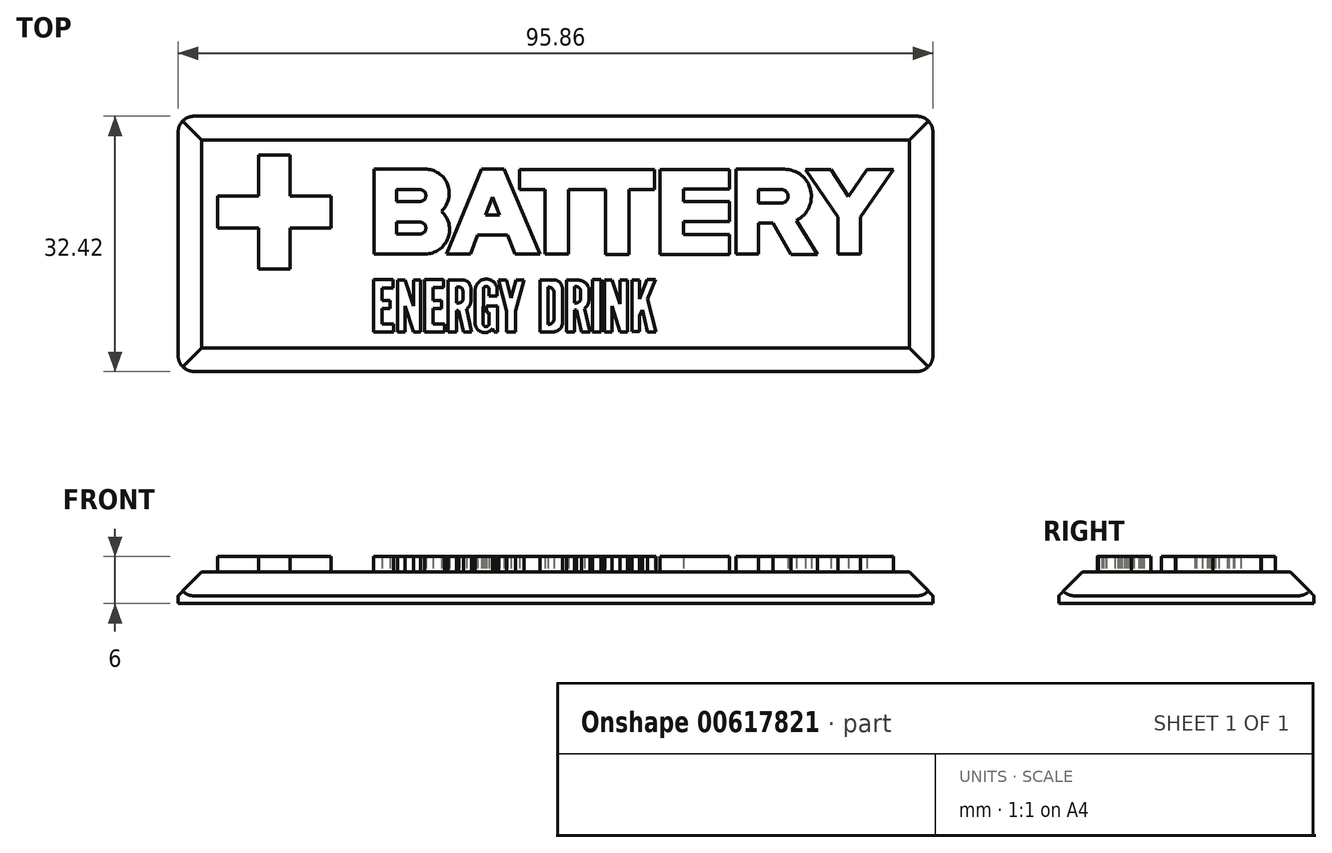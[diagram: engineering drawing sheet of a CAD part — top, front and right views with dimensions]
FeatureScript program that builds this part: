
annotation { "Feature Type Name" : "Feature", "Feature Type Description" : "" }
export const myFeature = defineFeature(function(context is Context, id is Id, definition is map)
    precondition{}
    {
        {
            var Q0;
            Q0=qCreatedBy(makeId("Top.planeOp"),FACE);
            var sketch = newSketch(context, id + "F0", { "sketchPlane" : qUnion([Q0])});
            skLineSegment(sketch, "E0", {"start": v(10.69, -9.1) * mm, "end": v(10.69, -11.17) * mm});
            skLineSegment(sketch, "E1", {"start": v(11.64, -4.52) * mm, "end": v(10.69, -7) * mm});
            skLineSegment(sketch, "E2", {"start": v(12.67, -4.52) * mm, "end": v(11.64, -4.52) * mm});
            skLineSegment(sketch, "E3", {"start": v(11.69, -7) * mm, "end": v(12.67, -4.52) * mm});
            skLineSegment(sketch, "E4", {"start": v(12.77, -11.18) * mm, "end": v(11.69, -7) * mm});
            skLineSegment(sketch, "E5", {"start": v(11.71, -11.18) * mm, "end": v(12.77, -11.18) * mm});
            skLineSegment(sketch, "E6", {"start": v(-14.22, -4.56) * mm, "end": v(-14.22, -5.55) * mm});
            skLineSegment(sketch, "E7", {"start": v(-15.55, -5.55) * mm, "end": v(-14.22, -5.55) * mm});
            skLineSegment(sketch, "E8", {"start": v(-15.55, -4.56) * mm, "end": v(-14.22, -4.56) * mm});
            skLineSegment(sketch, "E9", {"start": v(-15.55, -10.18) * mm, "end": v(-15.55, -8.23) * mm});
            skLineSegment(sketch, "E10", {"start": v(-16.65, -11.2) * mm, "end": v(-16.65, -4.56) * mm});
            skLineSegment(sketch, "E11", {"start": v(-16.65, -4.56) * mm, "end": v(-15.55, -4.56) * mm});
            skLineSegment(sketch, "E12", {"start": v(-16.65, -11.2) * mm, "end": v(-15.55, -11.2) * mm});
            skLineSegment(sketch, "E13", {"start": v(-22, -7.22) * mm, "end": v(-22, -5.58) * mm});
            skLineSegment(sketch, "E14", {"start": v(-18.07, -11.18) * mm, "end": v(-19.11, -7.88) * mm});
            skLineSegment(sketch, "E15", {"start": v(-19.11, -4.58) * mm, "end": v(-18.07, -7.88) * mm});
            skLineSegment(sketch, "E16", {"start": v(-17.12, -4.58) * mm, "end": v(-17.12, -11.18) * mm});
            skLineSegment(sketch, "E17", {"start": v(-18.07, -4.58) * mm, "end": v(-18.07, -7.88) * mm});
            skLineSegment(sketch, "E18", {"start": v(-18.07, -11.18) * mm, "end": v(-17.12, -11.18) * mm});
            skLineSegment(sketch, "E19", {"start": v(-18.07, -4.58) * mm, "end": v(-17.12, -4.58) * mm});
            skLineSegment(sketch, "E20", {"start": v(-20.06, -11.2) * mm, "end": v(-20.06, -4.58) * mm});
            skLineSegment(sketch, "E21", {"start": v(-19.11, -11.2) * mm, "end": v(-19.11, -7.88) * mm});
            skLineSegment(sketch, "E22", {"start": v(-19.11, -4.58) * mm, "end": v(-20.06, -4.58) * mm});
            skLineSegment(sketch, "E23", {"start": v(-19.11, -11.2) * mm, "end": v(-20.06, -11.2) * mm});
            skLineSegment(sketch, "E24", {"start": v(-20.6, -10.2) * mm, "end": v(-20.6, -11.2) * mm});
            skLineSegment(sketch, "E25", {"start": v(-22, -11.2) * mm, "end": v(-20.6, -11.2) * mm});
            skLineSegment(sketch, "E26", {"start": v(-22, -10.2) * mm, "end": v(-20.6, -10.2) * mm});
            skLineSegment(sketch, "E27", {"start": v(-21, -7.22) * mm, "end": v(-21, -8.23) * mm});
            skLineSegment(sketch, "E28", {"start": v(-22, -8.23) * mm, "end": v(-21, -8.23) * mm});
            skLineSegment(sketch, "E29", {"start": v(-22, -7.22) * mm, "end": v(-21, -7.22) * mm});
            skLineSegment(sketch, "E30", {"start": v(-20.64, -4.54) * mm, "end": v(-20.64, -5.58) * mm});
            skLineSegment(sketch, "E31", {"start": v(-22, -5.58) * mm, "end": v(-20.64, -5.58) * mm});
            skLineSegment(sketch, "E32", {"start": v(-22, -4.54) * mm, "end": v(-20.64, -4.54) * mm});
            skLineSegment(sketch, "E33", {"start": v(-22, -10.2) * mm, "end": v(-22, -8.23) * mm});
            skLineSegment(sketch, "E34", {"start": v(-23.13, -11.2) * mm, "end": v(-23.13, -4.54) * mm});
            skLineSegment(sketch, "E35", {"start": v(-23.13, -4.54) * mm, "end": v(-22, -4.54) * mm});
            skLineSegment(sketch, "E36", {"start": v(-23.13, -11.2) * mm, "end": v(-22, -11.2) * mm});
            skLineSegment(sketch, "E37", {"start": v(42.93, 9.45) * mm, "end": v(38.76, 3.38) * mm});
            skLineSegment(sketch, "E38", {"start": v(39.57, 9.45) * mm, "end": v(42.93, 9.45) * mm});
            skLineSegment(sketch, "E39", {"start": v(37.24, 6.03) * mm, "end": v(39.57, 9.45) * mm});
            skLineSegment(sketch, "E40", {"start": v(34.99, 9.43) * mm, "end": v(37.24, 6.03) * mm});
            skLineSegment(sketch, "E41", {"start": v(31.74, 9.43) * mm, "end": v(34.99, 9.43) * mm});
            skLineSegment(sketch, "E42", {"start": v(35.85, 3.38) * mm, "end": v(31.74, 9.43) * mm});
            skLineSegment(sketch, "E43", {"start": v(38.76, -1.31) * mm, "end": v(38.76, 3.38) * mm});
            skLineSegment(sketch, "E44", {"start": v(35.85, -1.31) * mm, "end": v(35.85, 3.38) * mm});
            skLineSegment(sketch, "E45", {"start": v(35.85, -1.31) * mm, "end": v(38.76, -1.31) * mm});
            skLineSegment(sketch, "E46", {"start": v(16.23, 5.4) * mm, "end": v(16.23, 6.94) * mm});
            skLineSegment(sketch, "E47", {"start": v(25.79, 2.66) * mm, "end": v(25.79, -1.3) * mm});
            skArc(sketch, "E48", {"start": v(30.6, 2.98) * mm, "mid": v(32.41, 6.83) * mm, "end": v(29.07, 9.47) * mm});
            skArc(sketch, "E49", {"start": v(28.7, 5.19) * mm, "mid": v(29.55, 6.04) * mm, "end": v(28.7, 6.89) * mm});
            skLineSegment(sketch, "E50", {"start": v(25.79, 9.47) * mm, "end": v(29.07, 9.47) * mm});
            skLineSegment(sketch, "E51", {"start": v(25.79, 6.89) * mm, "end": v(28.7, 6.89) * mm});
            skLineSegment(sketch, "E52", {"start": v(25.79, 5.19) * mm, "end": v(28.7, 5.19) * mm});
            skLineSegment(sketch, "E53", {"start": v(33.25, -1.36) * mm, "end": v(30.6, 2.98) * mm});
            skLineSegment(sketch, "E54", {"start": v(29.88, -1.36) * mm, "end": v(33.25, -1.36) * mm});
            skLineSegment(sketch, "E55", {"start": v(27.64, 2.66) * mm, "end": v(29.88, -1.36) * mm});
            skLineSegment(sketch, "E56", {"start": v(-1.32, 6.92) * mm, "end": v(-1.32, -1.32) * mm});
            skLineSegment(sketch, "E57", {"start": v(-1.32, -1.32) * mm, "end": v(1.64, -1.32) * mm});
            skLineSegment(sketch, "E58", {"start": v(12.57, 9.46) * mm, "end": v(12.57, 6.92) * mm});
            skLineSegment(sketch, "E59", {"start": v(-4.54, 9.46) * mm, "end": v(-4.54, 6.92) * mm});
            skLineSegment(sketch, "E60", {"start": v(-4.54, 6.92) * mm, "end": v(-1.32, 6.92) * mm});
            skLineSegment(sketch, "E61", {"start": v(-4.54, 9.46) * mm, "end": v(12.57, 9.46) * mm});
            skLineSegment(sketch, "E62", {"start": v(-8, 5.96) * mm, "end": v(-8.9, 3.66) * mm});
            skLineSegment(sketch, "E63", {"start": v(-7.12, 3.66) * mm, "end": v(-8, 5.96) * mm});
            skLineSegment(sketch, "E64", {"start": v(-8.9, 3.66) * mm, "end": v(-7.12, 3.66) * mm});
            skLineSegment(sketch, "E65", {"start": v(-9.36, 9.47) * mm, "end": v(-13.84, -1.29) * mm});
            skLineSegment(sketch, "E66", {"start": v(-6.55, 9.47) * mm, "end": v(-9.36, 9.47) * mm});
            skLineSegment(sketch, "E67", {"start": v(-1.94, -1.29) * mm, "end": v(-6.55, 9.47) * mm});
            skLineSegment(sketch, "E68", {"start": v(-20.16, 2.77) * mm, "end": v(-17.23, 2.77) * mm});
            skLineSegment(sketch, "E69", {"start": v(-20.16, 1.24) * mm, "end": v(-17.23, 1.24) * mm});
            skLineSegment(sketch, "E70", {"start": v(-20.16, 2.77) * mm, "end": v(-20.16, 1.24) * mm});
            skArc(sketch, "E71", {"start": v(-17.23, 5.37) * mm, "mid": v(-16.47, 6.13) * mm, "end": v(-17.23, 6.9) * mm});
            skArc(sketch, "E72", {"start": v(-17.23, 1.24) * mm, "mid": v(-16.47, 2) * mm, "end": v(-17.23, 2.77) * mm});
            skLineSegment(sketch, "E73", {"start": v(-13.84, -1.29) * mm, "end": v(-10.78, -1.29) * mm});
            skLineSegment(sketch, "E74", {"start": v(-10.78, -1.29) * mm, "end": v(-9.9, 1.1) * mm});
            skLineSegment(sketch, "E75", {"start": v(-9.9, 1.1) * mm, "end": v(-6.12, 1.1) * mm});
            skLineSegment(sketch, "E76", {"start": v(-6.12, 1.1) * mm, "end": v(-5.16, -1.29) * mm});
            skLineSegment(sketch, "E77", {"start": v(-5.16, -1.29) * mm, "end": v(-1.94, -1.29) * mm});
            skLineSegment(sketch, "E78", {"start": v(1.64, 6.92) * mm, "end": v(1.64, -1.32) * mm});
            skLineSegment(sketch, "E79", {"start": v(6.36, -1.37) * mm, "end": v(9.35, -1.37) * mm});
            skLineSegment(sketch, "E80", {"start": v(6.36, 6.92) * mm, "end": v(6.36, -1.37) * mm});
            skLineSegment(sketch, "E81", {"start": v(9.35, 6.92) * mm, "end": v(9.35, -1.37) * mm});
            skLineSegment(sketch, "E82", {"start": v(1.64, 6.92) * mm, "end": v(6.36, 6.92) * mm});
            skLineSegment(sketch, "E83", {"start": v(9.35, 6.92) * mm, "end": v(12.57, 6.92) * mm});
            skLineSegment(sketch, "E84", {"start": v(13.26, -1.37) * mm, "end": v(16.23, -1.37) * mm});
            skLineSegment(sketch, "E85", {"start": v(13.26, 9.47) * mm, "end": v(16.23, 9.47) * mm});
            skLineSegment(sketch, "E86", {"start": v(13.26, -1.37) * mm, "end": v(13.26, 9.47) * mm});
            skLineSegment(sketch, "E87", {"start": v(16.23, 1.2) * mm, "end": v(16.23, 2.87) * mm});
            skLineSegment(sketch, "E88", {"start": v(16.23, 9.47) * mm, "end": v(22.12, 9.47) * mm});
            skLineSegment(sketch, "E89", {"start": v(16.23, 6.94) * mm, "end": v(22.12, 6.94) * mm});
            skLineSegment(sketch, "E90", {"start": v(22.12, 9.47) * mm, "end": v(22.12, 6.94) * mm});
            skLineSegment(sketch, "E91", {"start": v(16.23, 5.4) * mm, "end": v(22.12, 5.4) * mm});
            skLineSegment(sketch, "E92", {"start": v(16.23, 2.87) * mm, "end": v(22.12, 2.87) * mm});
            skLineSegment(sketch, "E93", {"start": v(22.12, 5.4) * mm, "end": v(22.12, 2.87) * mm});
            skLineSegment(sketch, "E94", {"start": v(16.23, 1.2) * mm, "end": v(22.11, 1.2) * mm});
            skLineSegment(sketch, "E95", {"start": v(16.23, -1.37) * mm, "end": v(22.11, -1.37) * mm});
            skLineSegment(sketch, "E96", {"start": v(22.11, 1.2) * mm, "end": v(22.11, -1.37) * mm});
            skLineSegment(sketch, "E97", {"start": v(22.9, 9.47) * mm, "end": v(25.79, 9.47) * mm});
            skLineSegment(sketch, "E98", {"start": v(22.9, -1.3) * mm, "end": v(25.79, -1.3) * mm});
            skLineSegment(sketch, "E99", {"start": v(22.9, 9.47) * mm, "end": v(22.9, -1.3) * mm});
            skLineSegment(sketch, "E100", {"start": v(25.79, 6.89) * mm, "end": v(25.79, 5.19) * mm});
            skLineSegment(sketch, "E101", {"start": v(25.79, 2.66) * mm, "end": v(27.64, 2.66) * mm});
            skLineSegment(sketch, "E102", {"start": v(-15.55, -7.2) * mm, "end": v(-14.5, -7.2) * mm});
            skLineSegment(sketch, "E103", {"start": v(-15.55, -8.23) * mm, "end": v(-14.5, -8.23) * mm});
            skLineSegment(sketch, "E104", {"start": v(-14.5, -7.2) * mm, "end": v(-14.5, -8.23) * mm});
            skLineSegment(sketch, "E105", {"start": v(-15.55, -10.18) * mm, "end": v(-14.1, -10.18) * mm});
            skLineSegment(sketch, "E106", {"start": v(-15.58, -11.2) * mm, "end": v(-14.1, -11.2) * mm});
            skLineSegment(sketch, "E107", {"start": v(-14.1, -10.18) * mm, "end": v(-14.1, -11.2) * mm});
            skLineSegment(sketch, "E108", {"start": v(-15.55, -7.2) * mm, "end": v(-15.55, -5.55) * mm});
            skLineSegment(sketch, "E109", {"start": v(-13.67, -11.19) * mm, "end": v(-12.6, -11.19) * mm});
            skLineSegment(sketch, "E110", {"start": v(-13.67, -4.57) * mm, "end": v(-12.6, -4.57) * mm});
            skLineSegment(sketch, "E111", {"start": v(-13.67, -11.19) * mm, "end": v(-13.67, -4.57) * mm});
            skLineSegment(sketch, "E112", {"start": v(-12.6, -11.19) * mm, "end": v(-12.6, -8.44) * mm});
            skLineSegment(sketch, "E113", {"start": v(-12.6, -8.44) * mm, "end": v(-12.33, -8.44) * mm});
            skLineSegment(sketch, "E114", {"start": v(-12.33, -8.44) * mm, "end": v(-11.72, -11.2) * mm});
            skLineSegment(sketch, "E115", {"start": v(-11.72, -11.2) * mm, "end": v(-10.64, -11.2) * mm});
            skLineSegment(sketch, "E116", {"start": v(-10.64, -11.2) * mm, "end": v(-11.32, -8.23) * mm});
            skLineSegment(sketch, "E117", {"start": v(-12.6, -5.5) * mm, "end": v(-12.2, -5.5) * mm});
            skLineSegment(sketch, "E118", {"start": v(-12.6, -7.49) * mm, "end": v(-12.2, -7.49) * mm});
            skLineSegment(sketch, "E119", {"start": v(-12.6, -4.57) * mm, "end": v(-11.87, -4.57) * mm});
            skLineSegment(sketch, "E120", {"start": v(-11.78, -5.95) * mm, "end": v(-11.78, -6.97) * mm});
            skLineSegment(sketch, "E121", {"start": v(-10.75, -5.57) * mm, "end": v(-10.75, -7.26) * mm});
            skArc(sketch, "E122", {"start": v(-11.78, -5.95) * mm, "mid": v(-11.9, -5.64) * mm, "end": v(-12.2, -5.5) * mm});
            skArc(sketch, "E123", {"start": v(-12.2, -7.49) * mm, "mid": v(-11.87, -7.33) * mm, "end": v(-11.78, -6.97) * mm});
            skArc(sketch, "E124", {"start": v(-10.75, -5.57) * mm, "mid": v(-11.12, -4.86) * mm, "end": v(-11.87, -4.57) * mm});
            skArc(sketch, "E125", {"start": v(-11.32, -8.23) * mm, "mid": v(-10.9, -7.82) * mm, "end": v(-10.75, -7.26) * mm});
            skLineSegment(sketch, "E126", {"start": v(-10.2, -6.03) * mm, "end": v(-10.22, -10.06) * mm});
            skLineSegment(sketch, "E127", {"start": v(-9.17, -5.76) * mm, "end": v(-9.2, -10.14) * mm});
            skLineSegment(sketch, "E128", {"start": v(-8.43, -6.65) * mm, "end": v(-7.4, -6.65) * mm});
            skLineSegment(sketch, "E129", {"start": v(-8.43, -6.65) * mm, "end": v(-8.43, -5.76) * mm});
            skLineSegment(sketch, "E130", {"start": v(-7.4, -6.65) * mm, "end": v(-7.4, -5.89) * mm});
            skLineSegment(sketch, "E131", {"start": v(-8.78, -7.87) * mm, "end": v(-7.37, -7.87) * mm});
            skLineSegment(sketch, "E132", {"start": v(-8.78, -7.87) * mm, "end": v(-8.78, -8.72) * mm});
            skLineSegment(sketch, "E133", {"start": v(-7.37, -7.87) * mm, "end": v(-7.37, -8.72) * mm});
            skLineSegment(sketch, "E134", {"start": v(-7.37, -8.72) * mm, "end": v(-7.37, -10.14) * mm});
            skLineSegment(sketch, "E135", {"start": v(-8.44, -8.72) * mm, "end": v(-8.44, -10.14) * mm});
            skLineSegment(sketch, "E136", {"start": v(-7.8, -11.17) * mm, "end": v(-7.37, -11.17) * mm});
            skLineSegment(sketch, "E137", {"start": v(-7.37, -11.17) * mm, "end": v(-7.37, -10.14) * mm});
            skLineSegment(sketch, "E138", {"start": v(-7.8, -11.17) * mm, "end": v(-8, -10.74) * mm});
            skArc(sketch, "E139", {"start": v(-8.43, -5.76) * mm, "mid": v(-8.8, -5.39) * mm, "end": v(-9.17, -5.76) * mm});
            skArc(sketch, "E140", {"start": v(-7.4, -5.89) * mm, "mid": v(-8.88, -4.49) * mm, "end": v(-10.2, -6.03) * mm});
            skArc(sketch, "E141", {"start": v(-10.22, -10.06) * mm, "mid": v(-9.36, -11.23) * mm, "end": v(-8, -10.74) * mm});
            skArc(sketch, "E142", {"start": v(-9.2, -10.14) * mm, "mid": v(-8.81, -10.52) * mm, "end": v(-8.44, -10.14) * mm});
            skLineSegment(sketch, "E143", {"start": v(-12.6, -7.49) * mm, "end": v(-12.6, -5.5) * mm});
            skLineSegment(sketch, "E144", {"start": v(-8.78, -8.72) * mm, "end": v(-8.44, -8.72) * mm});
            skLineSegment(sketch, "E145", {"start": v(-6.21, -11.18) * mm, "end": v(-5.07, -11.18) * mm});
            skLineSegment(sketch, "E146", {"start": v(-6.21, -11.18) * mm, "end": v(-6.21, -8.52) * mm});
            skLineSegment(sketch, "E147", {"start": v(-5.07, -11.18) * mm, "end": v(-5.07, -8.52) * mm});
            skLineSegment(sketch, "E148", {"start": v(-6.21, -8.52) * mm, "end": v(-7.26, -4.6) * mm});
            skLineSegment(sketch, "E149", {"start": v(-7.26, -4.6) * mm, "end": v(-6.21, -4.6) * mm});
            skLineSegment(sketch, "E150", {"start": v(-6.21, -4.6) * mm, "end": v(-5.67, -6.88) * mm});
            skLineSegment(sketch, "E151", {"start": v(-5.67, -6.88) * mm, "end": v(-5.02, -4.57) * mm});
            skLineSegment(sketch, "E152", {"start": v(-5.02, -4.57) * mm, "end": v(-3.98, -4.57) * mm});
            skLineSegment(sketch, "E153", {"start": v(-3.98, -4.57) * mm, "end": v(-5.07, -8.52) * mm});
            skLineSegment(sketch, "E154", {"start": v(-1.98, -4.56) * mm, "end": v(-0.94, -4.56) * mm});
            skLineSegment(sketch, "E155", {"start": v(-1.98, -11.18) * mm, "end": v(-0.94, -11.18) * mm});
            skLineSegment(sketch, "E156", {"start": v(-1.98, -4.56) * mm, "end": v(-1.98, -11.18) * mm});
            skLineSegment(sketch, "E157", {"start": v(-0.94, -5.5) * mm, "end": v(-0.94, -10.22) * mm});
            skLineSegment(sketch, "E158", {"start": v(-0.2, -6.2) * mm, "end": v(-0.2, -9.54) * mm});
            skLineSegment(sketch, "E159", {"start": v(0.87, -5.81) * mm, "end": v(0.87, -10.19) * mm});
            skLineSegment(sketch, "E160", {"start": v(-0.94, -4.56) * mm, "end": v(-0.27, -4.56) * mm});
            skLineSegment(sketch, "E161", {"start": v(-0.94, -11.18) * mm, "end": v(-0.29, -11.18) * mm});
            skArc(sketch, "E162", {"start": v(-0.2, -6.2) * mm, "mid": v(-0.42, -5.68) * mm, "end": v(-0.94, -5.5) * mm});
            skArc(sketch, "E163", {"start": v(-0.94, -10.22) * mm, "mid": v(-0.42, -10.05) * mm, "end": v(-0.2, -9.54) * mm});
            skArc(sketch, "E164", {"start": v(0.87, -5.81) * mm, "mid": v(0.57, -4.94) * mm, "end": v(-0.27, -4.56) * mm});
            skArc(sketch, "E165", {"start": v(-0.29, -11.18) * mm, "mid": v(0.48, -10.9) * mm, "end": v(0.87, -10.19) * mm});
            skLineSegment(sketch, "E166", {"start": v(1.38, -4.61) * mm, "end": v(2.4, -4.61) * mm});
            skLineSegment(sketch, "E167", {"start": v(1.38, -11.2) * mm, "end": v(2.4, -11.2) * mm});
            skLineSegment(sketch, "E168", {"start": v(1.38, -4.61) * mm, "end": v(1.38, -11.2) * mm});
            skLineSegment(sketch, "E169", {"start": v(2.4, -5.45) * mm, "end": v(2.4, -7.5) * mm});
            skLineSegment(sketch, "E170", {"start": v(2.4, -8.4) * mm, "end": v(2.68, -8.4) * mm});
            skLineSegment(sketch, "E171", {"start": v(2.68, -8.4) * mm, "end": v(3.28, -11.18) * mm});
            skLineSegment(sketch, "E172", {"start": v(3.28, -11.18) * mm, "end": v(4.39, -11.18) * mm});
            skLineSegment(sketch, "E173", {"start": v(4.39, -11.18) * mm, "end": v(3.67, -8.2) * mm});
            skLineSegment(sketch, "E174", {"start": v(2.4, -5.45) * mm, "end": v(2.72, -5.45) * mm});
            skLineSegment(sketch, "E175", {"start": v(2.4, -7.5) * mm, "end": v(2.74, -7.5) * mm});
            skLineSegment(sketch, "E176", {"start": v(3.18, -5.97) * mm, "end": v(3.18, -6.98) * mm});
            skLineSegment(sketch, "E177", {"start": v(2.4, -4.61) * mm, "end": v(2.9, -4.61) * mm});
            skArc(sketch, "E178", {"start": v(3.18, -5.97) * mm, "mid": v(3.05, -5.62) * mm, "end": v(2.72, -5.45) * mm});
            skArc(sketch, "E179", {"start": v(2.74, -7.5) * mm, "mid": v(3.06, -7.32) * mm, "end": v(3.18, -6.98) * mm});
            skArc(sketch, "E180", {"start": v(4.23, -5.62) * mm, "mid": v(3.74, -4.9) * mm, "end": v(2.9, -4.61) * mm});
            skLineSegment(sketch, "E181", {"start": v(4.23, -5.62) * mm, "end": v(4.23, -7.16) * mm});
            skArc(sketch, "E182", {"start": v(3.67, -8.2) * mm, "mid": v(4.08, -7.75) * mm, "end": v(4.23, -7.16) * mm});
            skLineSegment(sketch, "E183", {"start": v(2.4, -8.4) * mm, "end": v(2.4, -11.2) * mm});
            skLineSegment(sketch, "E184", {"start": v(4.67, -4.52) * mm, "end": v(5.77, -4.52) * mm});
            skLineSegment(sketch, "E185", {"start": v(4.67, -11.2) * mm, "end": v(5.77, -11.2) * mm});
            skLineSegment(sketch, "E186", {"start": v(4.67, -4.52) * mm, "end": v(4.67, -11.2) * mm});
            skLineSegment(sketch, "E187", {"start": v(5.77, -4.52) * mm, "end": v(5.77, -11.2) * mm});
            skLineSegment(sketch, "E188", {"start": v(6.23, -4.57) * mm, "end": v(7.19, -4.57) * mm});
            skLineSegment(sketch, "E189", {"start": v(6.23, -11.2) * mm, "end": v(7.19, -11.2) * mm});
            skLineSegment(sketch, "E190", {"start": v(6.23, -4.57) * mm, "end": v(6.23, -11.2) * mm});
            skLineSegment(sketch, "E191", {"start": v(7.19, -7.89) * mm, "end": v(7.19, -11.2) * mm});
            skLineSegment(sketch, "E192", {"start": v(9.12, -11.18) * mm, "end": v(8.18, -11.18) * mm});
            skLineSegment(sketch, "E193", {"start": v(9.12, -4.57) * mm, "end": v(8.18, -4.57) * mm});
            skLineSegment(sketch, "E194", {"start": v(9.12, -11.18) * mm, "end": v(9.12, -4.57) * mm});
            skLineSegment(sketch, "E195", {"start": v(8.18, -7.67) * mm, "end": v(8.18, -4.57) * mm});
            skLineSegment(sketch, "E196", {"start": v(7.19, -4.57) * mm, "end": v(8.18, -7.67) * mm});
            skLineSegment(sketch, "E197", {"start": v(8.18, -11.18) * mm, "end": v(7.19, -7.89) * mm});
            skLineSegment(sketch, "E198", {"start": v(9.7, -4.6) * mm, "end": v(10.69, -4.6) * mm});
            skLineSegment(sketch, "E199", {"start": v(9.7, -11.17) * mm, "end": v(10.69, -11.17) * mm});
            skLineSegment(sketch, "E200", {"start": v(9.7, -4.6) * mm, "end": v(9.7, -11.17) * mm});
            skLineSegment(sketch, "E201", {"start": v(10.69, -4.6) * mm, "end": v(10.69, -7) * mm});
            skLineSegment(sketch, "E202", {"start": v(10.69, -9.1) * mm, "end": v(11.03, -8.39) * mm});
            skLineSegment(sketch, "E203", {"start": v(11.03, -8.39) * mm, "end": v(11.71, -11.18) * mm});
            skLineSegment(sketch, "E204", {"start": v(-37.74, 11.28) * mm, "end": v(-33.7, 11.28) * mm});
            skLineSegment(sketch, "E205", {"start": v(-37.74, -3.17) * mm, "end": v(-33.7, -3.17) * mm});
            skLineSegment(sketch, "E206", {"start": v(-37.74, 11.28) * mm, "end": v(-37.74, 6.07) * mm});
            skLineSegment(sketch, "E207", {"start": v(-33.7, 11.28) * mm, "end": v(-33.7, 6.07) * mm});
            skLineSegment(sketch, "E208", {"start": v(-42.93, 6.07) * mm, "end": v(-37.74, 6.07) * mm});
            skLineSegment(sketch, "E209", {"start": v(-42.93, 2.01) * mm, "end": v(-37.74, 2.01) * mm});
            skLineSegment(sketch, "E210", {"start": v(-42.93, 6.07) * mm, "end": v(-42.93, 2.01) * mm});
            skLineSegment(sketch, "E211", {"start": v(-28.5, 6.07) * mm, "end": v(-28.5, 2.01) * mm});
            skLineSegment(sketch, "E212", {"start": v(-33.7, 6.07) * mm, "end": v(-28.5, 6.07) * mm});
            skLineSegment(sketch, "E213", {"start": v(-37.74, 2.01) * mm, "end": v(-37.74, -3.17) * mm});
            skLineSegment(sketch, "E214", {"start": v(-33.7, 2.01) * mm, "end": v(-33.7, -3.17) * mm});
            skLineSegment(sketch, "E215", {"start": v(-33.7, 2.01) * mm, "end": v(-28.5, 2.01) * mm});
            skLineSegment(sketch, "E216", {"start": v(-23.07, 9.5) * mm, "end": v(-23.07, -1.29) * mm});
            skLineSegment(sketch, "E217", {"start": v(-23.07, -1.29) * mm, "end": v(-16.57, -1.29) * mm});
            skLineSegment(sketch, "E218", {"start": v(-23.07, 9.5) * mm, "end": v(-16.57, 9.5) * mm});
            skArc(sketch, "E219", {"start": v(-14.5, 4.15) * mm, "mid": v(-13.7, 7.54) * mm, "end": v(-16.57, 9.5) * mm});
            skArc(sketch, "E220", {"start": v(-16.57, -1.29) * mm, "mid": v(-13.66, 0.72) * mm, "end": v(-14.5, 4.15) * mm});
            skLineSegment(sketch, "E221", {"start": v(-20.16, 6.9) * mm, "end": v(-20.16, 5.37) * mm});
            skLineSegment(sketch, "E222", {"start": v(-20.16, 5.37) * mm, "end": v(-17.23, 5.37) * mm});
            skLineSegment(sketch, "E223", {"start": v(-20.16, 6.9) * mm, "end": v(-17.23, 6.9) * mm});
            skSolve(sketch);
        }
        {
            var Q0;
            Q0=qCreatedBy(makeId("Top.planeOp"),FACE);
            var sketch = newSketch(context, id + "F1", { "sketchPlane" : qUnion([Q0])});
            skLineSegment(sketch, "E224.bottom", {"start": v(47.93, -16.2) * mm, "end": v(-47.93, -16.2) * mm});
            skLineSegment(sketch, "E224.top", {"start": v(47.93, 16.2) * mm, "end": v(-47.93, 16.2) * mm});
            skLineSegment(sketch, "E224.left", {"start": v(47.93, -16.2) * mm, "end": v(47.93, 16.2) * mm});
            skLineSegment(sketch, "E224.right", {"start": v(-47.93, -16.2) * mm, "end": v(-47.93, 16.2) * mm});
            skPoint(sketch, "E224.middle", {"position": v(0, 0) * mm});
            skSolve(sketch);
        }
        {
            var Q0;
            Q0 = qSketchRegion(id + "F1", true);
            extrude(context, id + "F2", {"entities" : qUnion([Q0]), "oppositeDirection" : true, "depth" : 4 * mm, "offsetDistance" : 25 * mm});
        }
        {
            var Q0;
            Q0 = qSketchRegion(id + "F0", true);
            extrude(context, id + "F3", {"entities" : qUnion([Q0]), "operationType" : NewBodyOperationType.ADD, "depth" : 2 * mm, "offsetDistance" : 25 * mm});
        }
        {
            var Q0;
            Q0=makeQuery(id+"F2.opExtrude","CAP_EDGE",EDGE,{"disambiguationData":[OSD([sQuery(id+"F1.wireOp",EDGE,"E224.bottom")])],"isStart":true});
            var Q1;
            Q1=makeQuery(id+"F2.opExtrude","CAP_EDGE",EDGE,{"disambiguationData":[OSD([sQuery(id+"F1.wireOp",EDGE,"E224.left")])],"isStart":true});
            var Q2;
            Q2=makeQuery(id+"F2.opExtrude","CAP_EDGE",EDGE,{"disambiguationData":[OSD([sQuery(id+"F1.wireOp",EDGE,"E224.top")])],"isStart":true});
            var Q3;
            Q3=makeQuery(id+"F2.opExtrude","CAP_EDGE",EDGE,{"disambiguationData":[OSD([sQuery(id+"F1.wireOp",EDGE,"E224.right")])],"isStart":true});
            chamfer(context, id + "F4", {"entities" : qUnion([Q0, Q1, Q2, Q3]), "width" : 3 * mm, "tangentPropagation" : true});
        }
        {
            var Q0;
            Q0=makeQuery(id+"F2.opExtrude","SWEPT_EDGE",EDGE,{"disambiguationData":[OSD([sQuery(id+"F1.wireOp",EDGE,"E224.top"),sQuery(id+"F1.wireOp",EDGE,"E224.right")])]});
            var Q1;
            Q1=makeQuery(id+"F2.opExtrude","SWEPT_EDGE",EDGE,{"disambiguationData":[OSD([sQuery(id+"F1.wireOp",EDGE,"E224.top"),sQuery(id+"F1.wireOp",EDGE,"E224.left")])]});
            var Q2;
            Q2=makeQuery(id+"F2.opExtrude","SWEPT_EDGE",EDGE,{"disambiguationData":[OSD([sQuery(id+"F1.wireOp",EDGE,"E224.bottom"),sQuery(id+"F1.wireOp",EDGE,"E224.left")])]});
            var Q3;
            Q3=makeQuery(id+"F2.opExtrude","SWEPT_EDGE",EDGE,{"disambiguationData":[OSD([sQuery(id+"F1.wireOp",EDGE,"E224.bottom"),sQuery(id+"F1.wireOp",EDGE,"E224.right")])]});
            fillet(context, id + "F5", {"entities" : qUnion([Q0, Q1, Q2, Q3]), "radius" : 2 * mm, "tangentPropagation" : true, "allowEdgeOverflow" : false});
        }
    });
